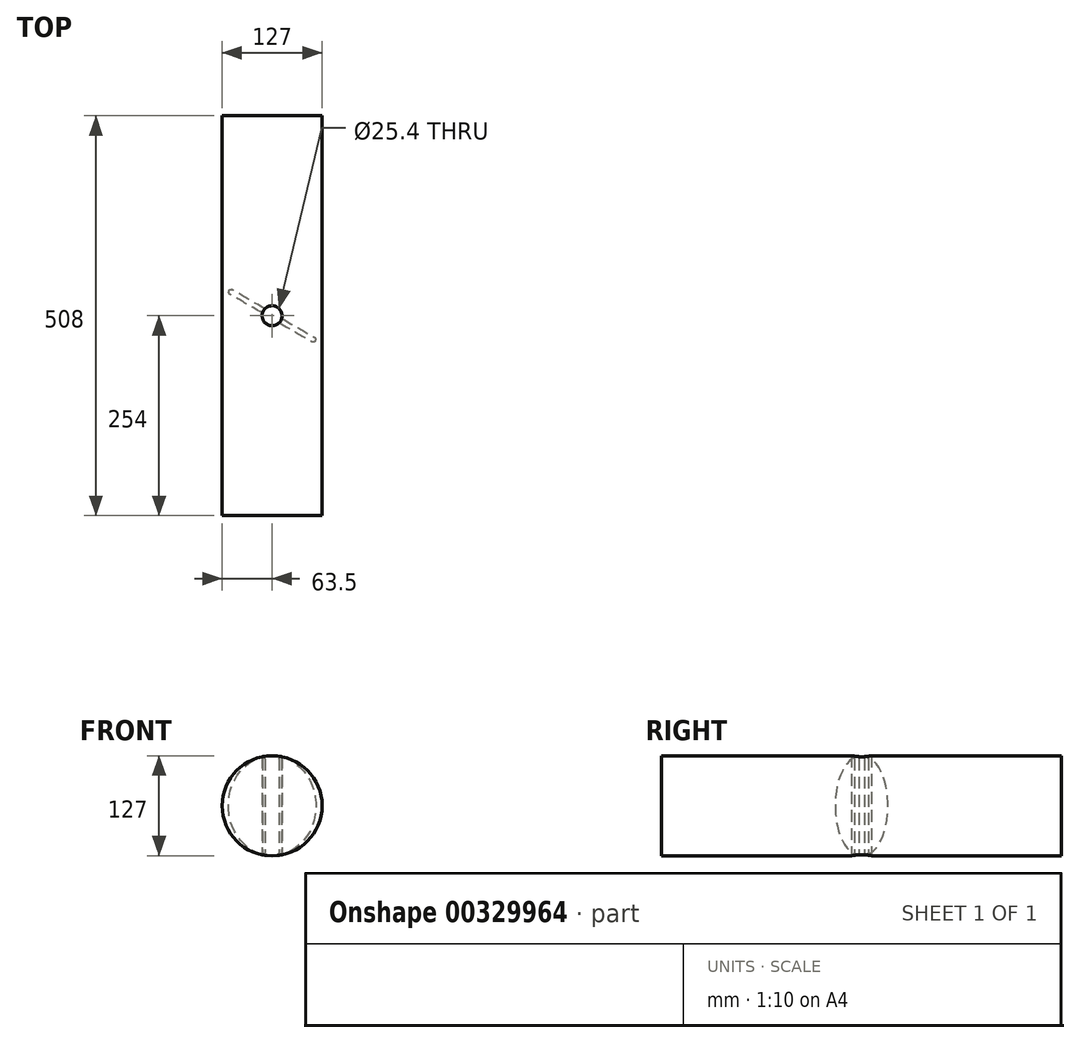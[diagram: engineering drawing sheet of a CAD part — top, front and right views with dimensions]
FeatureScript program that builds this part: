
annotation { "Feature Type Name" : "Feature", "Feature Type Description" : "" }
export const myFeature = defineFeature(function(context is Context, id is Id, definition is map)
    precondition{}
    {
        {
            var Q0;
            Q0=qCreatedBy(makeId("Front.planeOp"),FACE);
            var sketch = newSketch(context, id + "F0", { "sketchPlane" : qUnion([Q0])});
            skCircle(sketch, "E0", {"center": v(0, 0) * mm, "radius": 63.5 * mm});
            skSolve(sketch);
        }
        {
            var Q0;
            Q0=qCreatedBy(makeId("Top.planeOp"),FACE);
            var sketch = newSketch(context, id + "F1", { "sketchPlane" : qUnion([Q0])});
            skCircle(sketch, "E1", {"center": v(0, 0) * mm, "radius": 12.7 * mm});
            skSolve(sketch);
        }
        {
            var Q0;
            Q0 = qSketchRegion(id + "F1", true);
            extrude(context, id + "F2", {"entities" : qUnion([Q0]), "endBound" : BoundingType.SYMMETRIC, "depth" : 190.5 * mm});
        }
        {
            var Q0;
            Q0=makeQuery(id+"F0.imprint","IMPRINT",FACE,{"disambiguationData":[TD([[makeQuery(id+"F0.imprint","IMPRINT",EDGE,{"derivedFrom":sQuery(id+"F0.wireOp",EDGE,"E0")}),1.0]])]});
            extrude(context, id + "F3", {"entities" : qUnion([Q0]), "operationType" : NewBodyOperationType.ADD, "endBound" : BoundingType.SYMMETRIC, "depth" : 6.35 * mm});
        }
        {
            var Q0;
            Q0=makeQuery(id+"F3.boolean.opBoolean","SPLIT",EDGE,{"disambiguationData":[OD(0.0)],"derivedFrom":makeQuery(id+"F3.opExtrude","CAP_EDGE",EDGE,{"disambiguationData":[OSD([sQuery(id+"F0.wireOp",EDGE,"E0")])],"isStart":false})});
            var Q1;
            Q1=makeQuery(id+"F3.boolean.opBoolean","SPLIT",EDGE,{"disambiguationData":[OD(1.0)],"derivedFrom":makeQuery(id+"F3.opExtrude","CAP_EDGE",EDGE,{"disambiguationData":[OSD([sQuery(id+"F0.wireOp",EDGE,"E0")])],"isStart":false})});
            var Q2;
            Q2=makeQuery(id+"F3.boolean.opBoolean","SPLIT",EDGE,{"disambiguationData":[OD(1.0)],"derivedFrom":makeQuery(id+"F3.opExtrude","CAP_EDGE",EDGE,{"disambiguationData":[OSD([sQuery(id+"F0.wireOp",EDGE,"E0")])],"isStart":true})});
            var Q3;
            Q3=makeQuery(id+"F3.boolean.opBoolean","SPLIT",EDGE,{"disambiguationData":[OD(0.0)],"derivedFrom":makeQuery(id+"F3.opExtrude","CAP_EDGE",EDGE,{"disambiguationData":[OSD([sQuery(id+"F0.wireOp",EDGE,"E0")])],"isStart":true})});
            fillet(context, id + "F4", {"entities" : qUnion([Q0, Q1, Q2, Q3]), "radius" : 2.54 * mm, "tangentPropagation" : true, "allowEdgeOverflow" : false});
        }
        {
            var Q0;
            Q0=qCreatedBy(makeId("Front.planeOp"),FACE);
            var sketch = newSketch(context, id + "F5", { "sketchPlane" : qUnion([Q0])});
            skLineSegment(sketch, "E2", {"start": v(0, 76.5) * mm, "end": v(0, -77.52) * mm, "construction": true});
            skSolve(sketch);
        }
        {
            var Q0;
            Q0=makeQuery(id+"F2.opExtrude","SWEPT_BODY",BODY,{"disambiguationData":[OSD([sQuery(id+"F1.wireOp",EDGE,"E1")])]});
            var Q1;
            Q1=sQuery(id+"F5.wireOp",EDGE,"E2");
            transform(context, id + "F6", {"entities" : qUnion([Q0]), "transformType" : TransformType.ROTATION, "transformAxis" : qUnion([Q1]), "angle" : 30 * degree, "makeCopy" : false});
        }
        {
            var Q0;
            Q0=qCreatedBy(makeId("Front.planeOp"),FACE);
            var sketch = newSketch(context, id + "F7", { "sketchPlane" : qUnion([Q0])});
            skCircle(sketch, "E3", {"center": v(0, 0) * mm, "radius": 63.5 * mm});
            skSolve(sketch);
        }
        {
            var Q0;
            Q0=makeQuery(id+"F7.imprint","IMPRINT",FACE,{"disambiguationData":[TD([[makeQuery(id+"F7.imprint","IMPRINT",EDGE,{"derivedFrom":sQuery(id+"F7.wireOp",EDGE,"E3")}),1.0]])]});
            extrude(context, id + "F8", {"entities" : qUnion([Q0]), "endBound" : BoundingType.SYMMETRIC, "depth" : 508 * mm});
        }
        {
            var Q0;
            Q0=makeQuery(id+"F2.opExtrude","SWEPT_BODY",BODY,{"disambiguationData":[OSD([sQuery(id+"F1.wireOp",EDGE,"E1")])]});
            var Q1;
            Q1=makeQuery(id+"F8.opExtrude","SWEPT_BODY",BODY,{"disambiguationData":[OSD([sQuery(id+"F7.wireOp",EDGE,"E3")])]});
            booleanBodies(context, id + "F9", {"operationType" : BooleanOperationType.SUBTRACTION, "tools" : qUnion([Q0]), "targets" : qUnion([Q1])});
        }
    });
